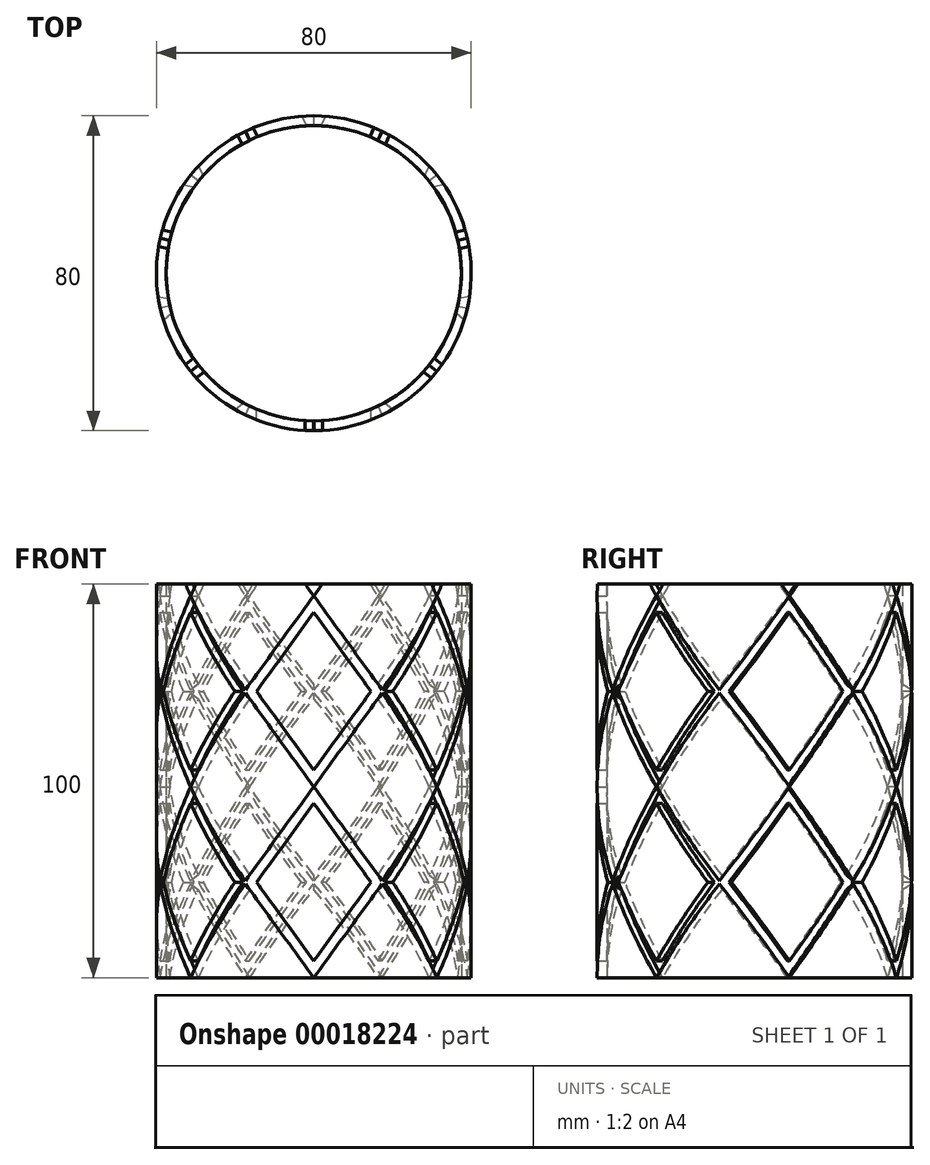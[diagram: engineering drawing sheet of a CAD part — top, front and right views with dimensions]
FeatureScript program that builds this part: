
annotation { "Feature Type Name" : "Feature", "Feature Type Description" : "" }
export const myFeature = defineFeature(function(context is Context, id is Id, definition is map)
    precondition{}
    {
        {
            var Q0;
            Q0=qCreatedBy(makeId("Top.planeOp"),FACE);
            var sketch = newSketch(context, id + "F0", { "sketchPlane" : qUnion([Q0])});
            skCircle(sketch, "E0", {"center": v(0, 0) * mm, "radius": 40 * mm});
            skCircle(sketch, "E1", {"center": v(0, 0) * mm, "radius": 37.5 * mm});
            skSolve(sketch);
        }
        {
            var Q0;
            Q0=makeQuery(id+"F0.imprint","IMPRINT",FACE,{"disambiguationData":[TD([[makeQuery(id+"F0.imprint","IMPRINT",EDGE,{"derivedFrom":sQuery(id+"F0.wireOp",EDGE,"E0")}),1.0]])]});
            extrude(context, id + "F1", {"entities" : qUnion([Q0]), "depth" : 100 * mm});
        }
        {
            var Q0;
            Q0=qCreatedBy(makeId("Front.planeOp"),FACE);
            var sketch = newSketch(context, id + "F2", { "sketchPlane" : qUnion([Q0])});
            skLineSegment(sketch, "E2", {"start": v(0, 0) * mm, "end": v(-17.65, 24.26) * mm});
            skLineSegment(sketch, "E3", {"start": v(-17.65, 24.26) * mm, "end": v(0, 48.52) * mm});
            skLineSegment(sketch, "E4", {"start": v(0, 48.52) * mm, "end": v(17.65, 24.26) * mm});
            skLineSegment(sketch, "E5", {"start": v(17.65, 24.26) * mm, "end": v(0, 0) * mm});
            skLineSegment(sketch, "E6.0", {"start": v(-14.55, 24.26) * mm, "end": v(0, 44.27) * mm});
            skLineSegment(sketch, "E6.1", {"start": v(0, 4.25) * mm, "end": v(-14.55, 24.26) * mm});
            skLineSegment(sketch, "E6.2", {"start": v(14.55, 24.26) * mm, "end": v(0, 4.25) * mm});
            skLineSegment(sketch, "E6.3", {"start": v(0, 44.27) * mm, "end": v(14.55, 24.26) * mm});
            skLineSegment(sketch, "E7.0.1.0", {"start": v(0, 97.02) * mm, "end": v(17.65, 72.76) * mm});
            skLineSegment(sketch, "E7.0.1.1", {"start": v(-17.65, 72.76) * mm, "end": v(0, 97.02) * mm});
            skLineSegment(sketch, "E7.0.1.2", {"start": v(0, 48.5) * mm, "end": v(-17.65, 72.76) * mm});
            skLineSegment(sketch, "E7.0.1.3", {"start": v(17.65, 72.76) * mm, "end": v(0, 48.5) * mm});
            skLineSegment(sketch, "E7.0.1.4", {"start": v(14.55, 72.76) * mm, "end": v(0, 52.75) * mm});
            skLineSegment(sketch, "E7.0.1.5", {"start": v(0, 92.77) * mm, "end": v(14.55, 72.76) * mm});
            skLineSegment(sketch, "E7.0.1.6", {"start": v(-14.55, 72.76) * mm, "end": v(0, 92.77) * mm});
            skLineSegment(sketch, "E7.0.1.7", {"start": v(0, 52.75) * mm, "end": v(-14.55, 72.76) * mm});
            skLineSegment(sketch, "E7.0.2.0", {"start": v(0, 145.52) * mm, "end": v(17.65, 121.26) * mm});
            skLineSegment(sketch, "E7.0.2.1", {"start": v(-17.65, 121.26) * mm, "end": v(0, 145.52) * mm});
            skLineSegment(sketch, "E7.0.2.2", {"start": v(0, 97) * mm, "end": v(-17.65, 121.26) * mm});
            skLineSegment(sketch, "E7.0.2.3", {"start": v(17.65, 121.26) * mm, "end": v(0, 97) * mm});
            skLineSegment(sketch, "E7.0.2.4", {"start": v(14.55, 121.26) * mm, "end": v(0, 101.25) * mm});
            skLineSegment(sketch, "E7.0.2.5", {"start": v(0, 141.27) * mm, "end": v(14.55, 121.26) * mm});
            skLineSegment(sketch, "E7.0.2.6", {"start": v(-14.55, 121.26) * mm, "end": v(0, 141.27) * mm});
            skLineSegment(sketch, "E7.0.2.7", {"start": v(0, 101.25) * mm, "end": v(-14.55, 121.26) * mm});
            skLineSegment(sketch, "E7.direction1", {"start": v(17.65, 24.26) * mm, "end": v(42.58, 24.26) * mm, "construction": true});
            skLineSegment(sketch, "E7.direction2", {"start": v(17.65, 24.26) * mm, "end": v(17.65, 72.76) * mm, "construction": true});
            skSolve(sketch);
        }
        {
            var Q0;
            Q0 = qSketchRegion(id + "F2", true);
            var Q1;
            Q1=makeQuery(id+"F1.opExtrude","SWEPT_FACE",FACE,{"disambiguationData":[OSD([sQuery(id+"F0.wireOp",EDGE,"E0")])]});
            extrude(context, id + "F3", {"entities" : qUnion([Q0]), "endBound" : BoundingType.UP_TO_SURFACE, "endBoundEntityFace" : qUnion([Q1]), "depth" : 25 * mm});
        }
        {
            var Q0;
            Q0=makeQuery(id+"F3.opExtrude","SWEPT_BODY",BODY,{"disambiguationData":[OSD([sQuery(id+"F2.wireOp",EDGE,"E2"),sQuery(id+"F2.wireOp",EDGE,"E3"),sQuery(id+"F2.wireOp",EDGE,"E4"),sQuery(id+"F2.wireOp",EDGE,"E5"),sQuery(id+"F2.wireOp",EDGE,"E6.0"),sQuery(id+"F2.wireOp",EDGE,"E6.1"),sQuery(id+"F2.wireOp",EDGE,"E6.2"),sQuery(id+"F2.wireOp",EDGE,"E6.3"),sQuery(id+"F2.wireOp",EDGE,"E7.0.1.0"),sQuery(id+"F2.wireOp",EDGE,"E7.0.1.1"),sQuery(id+"F2.wireOp",EDGE,"E7.0.1.2"),sQuery(id+"F2.wireOp",EDGE,"E7.0.1.3"),sQuery(id+"F2.wireOp",EDGE,"E7.0.1.4"),sQuery(id+"F2.wireOp",EDGE,"E7.0.1.5"),sQuery(id+"F2.wireOp",EDGE,"E7.0.1.6"),sQuery(id+"F2.wireOp",EDGE,"E7.0.1.7"),sQuery(id+"F2.wireOp",EDGE,"E7.0.2.0"),sQuery(id+"F2.wireOp",EDGE,"E7.0.2.1"),sQuery(id+"F2.wireOp",EDGE,"E7.0.2.2"),sQuery(id+"F2.wireOp",EDGE,"E7.0.2.3"),sQuery(id+"F2.wireOp",EDGE,"E7.0.2.4"),sQuery(id+"F2.wireOp",EDGE,"E7.0.2.5"),sQuery(id+"F2.wireOp",EDGE,"E7.0.2.6"),sQuery(id+"F2.wireOp",EDGE,"E7.0.2.7")])]});
            var Q1;
            Q1=makeQuery(id+"F1.opExtrude","CAP_EDGE",EDGE,{"disambiguationData":[OSD([sQuery(id+"F0.wireOp",EDGE,"E0")])],"isStart":false});
            circularPattern(context, id + "F4", {"entities" : qUnion([Q0]), "axis" : qUnion([Q1]), "angle" : 360 * degree, "instanceCount" : 7, "equalSpace" : true});
        }
        {
            var Q0;
            Q0=makeQuery(id+"F3.opExtrude","SWEPT_BODY",BODY,{"disambiguationData":[OSD([sQuery(id+"F2.wireOp",EDGE,"E2"),sQuery(id+"F2.wireOp",EDGE,"E3"),sQuery(id+"F2.wireOp",EDGE,"E4"),sQuery(id+"F2.wireOp",EDGE,"E5"),sQuery(id+"F2.wireOp",EDGE,"E6.0"),sQuery(id+"F2.wireOp",EDGE,"E6.1"),sQuery(id+"F2.wireOp",EDGE,"E6.2"),sQuery(id+"F2.wireOp",EDGE,"E6.3"),sQuery(id+"F2.wireOp",EDGE,"E7.0.1.0"),sQuery(id+"F2.wireOp",EDGE,"E7.0.1.1"),sQuery(id+"F2.wireOp",EDGE,"E7.0.1.2"),sQuery(id+"F2.wireOp",EDGE,"E7.0.1.3"),sQuery(id+"F2.wireOp",EDGE,"E7.0.1.4"),sQuery(id+"F2.wireOp",EDGE,"E7.0.1.5"),sQuery(id+"F2.wireOp",EDGE,"E7.0.1.6"),sQuery(id+"F2.wireOp",EDGE,"E7.0.1.7"),sQuery(id+"F2.wireOp",EDGE,"E7.0.2.0"),sQuery(id+"F2.wireOp",EDGE,"E7.0.2.1"),sQuery(id+"F2.wireOp",EDGE,"E7.0.2.2"),sQuery(id+"F2.wireOp",EDGE,"E7.0.2.3"),sQuery(id+"F2.wireOp",EDGE,"E7.0.2.4"),sQuery(id+"F2.wireOp",EDGE,"E7.0.2.5"),sQuery(id+"F2.wireOp",EDGE,"E7.0.2.6"),sQuery(id+"F2.wireOp",EDGE,"E7.0.2.7")])]});
            var Q1;
            Q1=makeQuery(id+"F4.opPattern","COPY",BODY,{"derivedFrom":makeQuery(id+"F3.opExtrude","SWEPT_BODY",BODY,{"disambiguationData":[OSD([sQuery(id+"F2.wireOp",EDGE,"E2"),sQuery(id+"F2.wireOp",EDGE,"E3"),sQuery(id+"F2.wireOp",EDGE,"E4"),sQuery(id+"F2.wireOp",EDGE,"E5"),sQuery(id+"F2.wireOp",EDGE,"E6.0"),sQuery(id+"F2.wireOp",EDGE,"E6.1"),sQuery(id+"F2.wireOp",EDGE,"E6.2"),sQuery(id+"F2.wireOp",EDGE,"E6.3"),sQuery(id+"F2.wireOp",EDGE,"E7.0.1.0"),sQuery(id+"F2.wireOp",EDGE,"E7.0.1.1"),sQuery(id+"F2.wireOp",EDGE,"E7.0.1.2"),sQuery(id+"F2.wireOp",EDGE,"E7.0.1.3"),sQuery(id+"F2.wireOp",EDGE,"E7.0.1.4"),sQuery(id+"F2.wireOp",EDGE,"E7.0.1.5"),sQuery(id+"F2.wireOp",EDGE,"E7.0.1.6"),sQuery(id+"F2.wireOp",EDGE,"E7.0.1.7"),sQuery(id+"F2.wireOp",EDGE,"E7.0.2.0"),sQuery(id+"F2.wireOp",EDGE,"E7.0.2.1"),sQuery(id+"F2.wireOp",EDGE,"E7.0.2.2"),sQuery(id+"F2.wireOp",EDGE,"E7.0.2.3"),sQuery(id+"F2.wireOp",EDGE,"E7.0.2.4"),sQuery(id+"F2.wireOp",EDGE,"E7.0.2.5"),sQuery(id+"F2.wireOp",EDGE,"E7.0.2.6"),sQuery(id+"F2.wireOp",EDGE,"E7.0.2.7")])]}),"instanceName":"1"});
            var Q2;
            Q2=makeQuery(id+"F4.opPattern","COPY",BODY,{"derivedFrom":makeQuery(id+"F3.opExtrude","SWEPT_BODY",BODY,{"disambiguationData":[OSD([sQuery(id+"F2.wireOp",EDGE,"E2"),sQuery(id+"F2.wireOp",EDGE,"E3"),sQuery(id+"F2.wireOp",EDGE,"E4"),sQuery(id+"F2.wireOp",EDGE,"E5"),sQuery(id+"F2.wireOp",EDGE,"E6.0"),sQuery(id+"F2.wireOp",EDGE,"E6.1"),sQuery(id+"F2.wireOp",EDGE,"E6.2"),sQuery(id+"F2.wireOp",EDGE,"E6.3"),sQuery(id+"F2.wireOp",EDGE,"E7.0.1.0"),sQuery(id+"F2.wireOp",EDGE,"E7.0.1.1"),sQuery(id+"F2.wireOp",EDGE,"E7.0.1.2"),sQuery(id+"F2.wireOp",EDGE,"E7.0.1.3"),sQuery(id+"F2.wireOp",EDGE,"E7.0.1.4"),sQuery(id+"F2.wireOp",EDGE,"E7.0.1.5"),sQuery(id+"F2.wireOp",EDGE,"E7.0.1.6"),sQuery(id+"F2.wireOp",EDGE,"E7.0.1.7"),sQuery(id+"F2.wireOp",EDGE,"E7.0.2.0"),sQuery(id+"F2.wireOp",EDGE,"E7.0.2.1"),sQuery(id+"F2.wireOp",EDGE,"E7.0.2.2"),sQuery(id+"F2.wireOp",EDGE,"E7.0.2.3"),sQuery(id+"F2.wireOp",EDGE,"E7.0.2.4"),sQuery(id+"F2.wireOp",EDGE,"E7.0.2.5"),sQuery(id+"F2.wireOp",EDGE,"E7.0.2.6"),sQuery(id+"F2.wireOp",EDGE,"E7.0.2.7")])]}),"instanceName":"2"});
            var Q3;
            Q3=makeQuery(id+"F4.opPattern","COPY",BODY,{"derivedFrom":makeQuery(id+"F3.opExtrude","SWEPT_BODY",BODY,{"disambiguationData":[OSD([sQuery(id+"F2.wireOp",EDGE,"E2"),sQuery(id+"F2.wireOp",EDGE,"E3"),sQuery(id+"F2.wireOp",EDGE,"E4"),sQuery(id+"F2.wireOp",EDGE,"E5"),sQuery(id+"F2.wireOp",EDGE,"E6.0"),sQuery(id+"F2.wireOp",EDGE,"E6.1"),sQuery(id+"F2.wireOp",EDGE,"E6.2"),sQuery(id+"F2.wireOp",EDGE,"E6.3"),sQuery(id+"F2.wireOp",EDGE,"E7.0.1.0"),sQuery(id+"F2.wireOp",EDGE,"E7.0.1.1"),sQuery(id+"F2.wireOp",EDGE,"E7.0.1.2"),sQuery(id+"F2.wireOp",EDGE,"E7.0.1.3"),sQuery(id+"F2.wireOp",EDGE,"E7.0.1.4"),sQuery(id+"F2.wireOp",EDGE,"E7.0.1.5"),sQuery(id+"F2.wireOp",EDGE,"E7.0.1.6"),sQuery(id+"F2.wireOp",EDGE,"E7.0.1.7"),sQuery(id+"F2.wireOp",EDGE,"E7.0.2.0"),sQuery(id+"F2.wireOp",EDGE,"E7.0.2.1"),sQuery(id+"F2.wireOp",EDGE,"E7.0.2.2"),sQuery(id+"F2.wireOp",EDGE,"E7.0.2.3"),sQuery(id+"F2.wireOp",EDGE,"E7.0.2.4"),sQuery(id+"F2.wireOp",EDGE,"E7.0.2.5"),sQuery(id+"F2.wireOp",EDGE,"E7.0.2.6"),sQuery(id+"F2.wireOp",EDGE,"E7.0.2.7")])]}),"instanceName":"3"});
            var Q4;
            Q4=makeQuery(id+"F4.opPattern","COPY",BODY,{"derivedFrom":makeQuery(id+"F3.opExtrude","SWEPT_BODY",BODY,{"disambiguationData":[OSD([sQuery(id+"F2.wireOp",EDGE,"E2"),sQuery(id+"F2.wireOp",EDGE,"E3"),sQuery(id+"F2.wireOp",EDGE,"E4"),sQuery(id+"F2.wireOp",EDGE,"E5"),sQuery(id+"F2.wireOp",EDGE,"E6.0"),sQuery(id+"F2.wireOp",EDGE,"E6.1"),sQuery(id+"F2.wireOp",EDGE,"E6.2"),sQuery(id+"F2.wireOp",EDGE,"E6.3"),sQuery(id+"F2.wireOp",EDGE,"E7.0.1.0"),sQuery(id+"F2.wireOp",EDGE,"E7.0.1.1"),sQuery(id+"F2.wireOp",EDGE,"E7.0.1.2"),sQuery(id+"F2.wireOp",EDGE,"E7.0.1.3"),sQuery(id+"F2.wireOp",EDGE,"E7.0.1.4"),sQuery(id+"F2.wireOp",EDGE,"E7.0.1.5"),sQuery(id+"F2.wireOp",EDGE,"E7.0.1.6"),sQuery(id+"F2.wireOp",EDGE,"E7.0.1.7"),sQuery(id+"F2.wireOp",EDGE,"E7.0.2.0"),sQuery(id+"F2.wireOp",EDGE,"E7.0.2.1"),sQuery(id+"F2.wireOp",EDGE,"E7.0.2.2"),sQuery(id+"F2.wireOp",EDGE,"E7.0.2.3"),sQuery(id+"F2.wireOp",EDGE,"E7.0.2.4"),sQuery(id+"F2.wireOp",EDGE,"E7.0.2.5"),sQuery(id+"F2.wireOp",EDGE,"E7.0.2.6"),sQuery(id+"F2.wireOp",EDGE,"E7.0.2.7")])]}),"instanceName":"4"});
            var Q5;
            Q5=makeQuery(id+"F4.opPattern","COPY",BODY,{"derivedFrom":makeQuery(id+"F3.opExtrude","SWEPT_BODY",BODY,{"disambiguationData":[OSD([sQuery(id+"F2.wireOp",EDGE,"E2"),sQuery(id+"F2.wireOp",EDGE,"E3"),sQuery(id+"F2.wireOp",EDGE,"E4"),sQuery(id+"F2.wireOp",EDGE,"E5"),sQuery(id+"F2.wireOp",EDGE,"E6.0"),sQuery(id+"F2.wireOp",EDGE,"E6.1"),sQuery(id+"F2.wireOp",EDGE,"E6.2"),sQuery(id+"F2.wireOp",EDGE,"E6.3"),sQuery(id+"F2.wireOp",EDGE,"E7.0.1.0"),sQuery(id+"F2.wireOp",EDGE,"E7.0.1.1"),sQuery(id+"F2.wireOp",EDGE,"E7.0.1.2"),sQuery(id+"F2.wireOp",EDGE,"E7.0.1.3"),sQuery(id+"F2.wireOp",EDGE,"E7.0.1.4"),sQuery(id+"F2.wireOp",EDGE,"E7.0.1.5"),sQuery(id+"F2.wireOp",EDGE,"E7.0.1.6"),sQuery(id+"F2.wireOp",EDGE,"E7.0.1.7"),sQuery(id+"F2.wireOp",EDGE,"E7.0.2.0"),sQuery(id+"F2.wireOp",EDGE,"E7.0.2.1"),sQuery(id+"F2.wireOp",EDGE,"E7.0.2.2"),sQuery(id+"F2.wireOp",EDGE,"E7.0.2.3"),sQuery(id+"F2.wireOp",EDGE,"E7.0.2.4"),sQuery(id+"F2.wireOp",EDGE,"E7.0.2.5"),sQuery(id+"F2.wireOp",EDGE,"E7.0.2.6"),sQuery(id+"F2.wireOp",EDGE,"E7.0.2.7")])]}),"instanceName":"5"});
            var Q6;
            Q6=makeQuery(id+"F4.opPattern","COPY",BODY,{"derivedFrom":makeQuery(id+"F3.opExtrude","SWEPT_BODY",BODY,{"disambiguationData":[OSD([sQuery(id+"F2.wireOp",EDGE,"E2"),sQuery(id+"F2.wireOp",EDGE,"E3"),sQuery(id+"F2.wireOp",EDGE,"E4"),sQuery(id+"F2.wireOp",EDGE,"E5"),sQuery(id+"F2.wireOp",EDGE,"E6.0"),sQuery(id+"F2.wireOp",EDGE,"E6.1"),sQuery(id+"F2.wireOp",EDGE,"E6.2"),sQuery(id+"F2.wireOp",EDGE,"E6.3"),sQuery(id+"F2.wireOp",EDGE,"E7.0.1.0"),sQuery(id+"F2.wireOp",EDGE,"E7.0.1.1"),sQuery(id+"F2.wireOp",EDGE,"E7.0.1.2"),sQuery(id+"F2.wireOp",EDGE,"E7.0.1.3"),sQuery(id+"F2.wireOp",EDGE,"E7.0.1.4"),sQuery(id+"F2.wireOp",EDGE,"E7.0.1.5"),sQuery(id+"F2.wireOp",EDGE,"E7.0.1.6"),sQuery(id+"F2.wireOp",EDGE,"E7.0.1.7"),sQuery(id+"F2.wireOp",EDGE,"E7.0.2.0"),sQuery(id+"F2.wireOp",EDGE,"E7.0.2.1"),sQuery(id+"F2.wireOp",EDGE,"E7.0.2.2"),sQuery(id+"F2.wireOp",EDGE,"E7.0.2.3"),sQuery(id+"F2.wireOp",EDGE,"E7.0.2.4"),sQuery(id+"F2.wireOp",EDGE,"E7.0.2.5"),sQuery(id+"F2.wireOp",EDGE,"E7.0.2.6"),sQuery(id+"F2.wireOp",EDGE,"E7.0.2.7")])]}),"instanceName":"6"});
            var Q7;
            Q7=makeQuery(id+"F1.opExtrude","SWEPT_BODY",BODY,{"disambiguationData":[OSD([sQuery(id+"F0.wireOp",EDGE,"E0"),sQuery(id+"F0.wireOp",EDGE,"E1")])]});
            booleanBodies(context, id + "F5", {"operationType" : BooleanOperationType.SUBTRACTION, "tools" : qUnion([Q0, Q1, Q2, Q3, Q4, Q5, Q6]), "targets" : qUnion([Q7])});
        }
        {
            var Q0;
            Q0=makeQuery(id+"F0.imprint","IMPRINT",FACE,{"disambiguationData":[TD([[makeQuery(id+"F0.imprint","IMPRINT",EDGE,{"derivedFrom":sQuery(id+"F0.wireOp",EDGE,"E1")}),1.0]])]});
            extrude(context, id + "F6", {"entities" : qUnion([Q0]), "depth" : 100 * mm});
        }
    });
